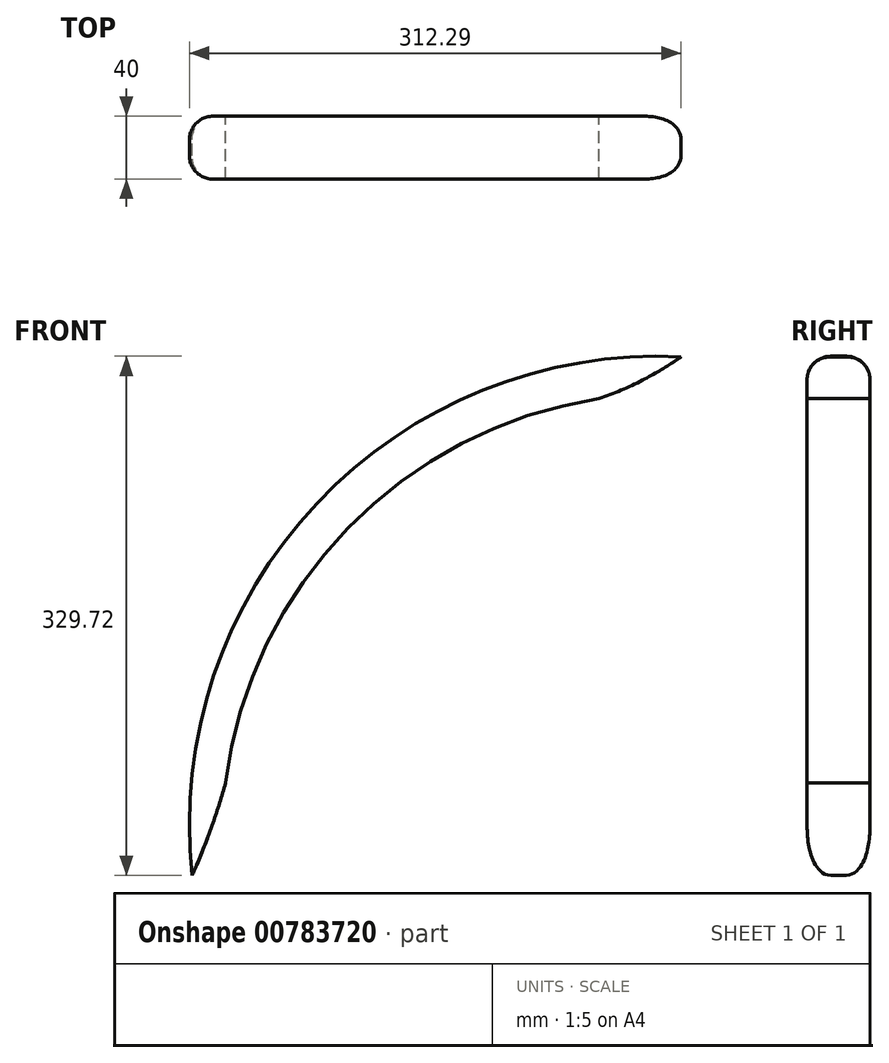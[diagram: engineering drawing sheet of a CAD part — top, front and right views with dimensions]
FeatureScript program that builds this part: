
annotation { "Feature Type Name" : "Feature", "Feature Type Description" : "" }
export const myFeature = defineFeature(function(context is Context, id is Id, definition is map)
    precondition{}
    {
        {
            var Q0;
            Q0=qCreatedBy(makeId("Front.planeOp"),FACE);
            var sketch = newSketch(context, id + "F0", { "sketchPlane" : qUnion([Q0])});
            skArc(sketch, "E0", {"start": v(-39.78, 269.99) * mm, "mid": v(-12.78, 281.45) * mm, "end": v(12.34, 296.57) * mm});
            skArc(sketch, "E1", {"start": v(-39.78, 269.99) * mm, "mid": v(-199.26, 187.75) * mm, "end": v(-276.9, 25.99) * mm});
            skArc(sketch, "E2", {"start": v(-298.2, -32.78) * mm, "mid": v(-286.5, -3.78) * mm, "end": v(-276.9, 25.99) * mm});
            skArc(sketch, "E3", {"start": v(12.34, 296.57) * mm, "mid": v(-218.9, 203.52) * mm, "end": v(-298.2, -32.78) * mm});
            skSolve(sketch);
        }
        {
            var Q0;
            Q0=makeQuery(id+"F0.imprint","IMPRINT",FACE,{"disambiguationData":[TD([[makeQuery(id+"F0.imprint","IMPRINT",EDGE,{"derivedFrom":sQuery(id+"F0.wireOp",EDGE,"E0")}),1.0]])]});
            extrude(context, id + "F1", {"entities" : qUnion([Q0]), "depth" : 40 * mm, "offsetDistance" : 25 * mm});
        }
        {
            var Q0;
            Q0=makeQuery(id+"F1.opExtrude","CAP_EDGE",EDGE,{"disambiguationData":[OSD([sQuery(id+"F0.wireOp",EDGE,"E3")])],"isStart":true});
            var Q1;
            Q1=makeQuery(id+"F1.opExtrude","CAP_EDGE",EDGE,{"disambiguationData":[OSD([sQuery(id+"F0.wireOp",EDGE,"E3")])],"isStart":false});
            fillet(context, id + "F2", {"entities" : qUnion([Q0, Q1]), "radius" : 15 * mm, "tangentPropagation" : true, "allowEdgeOverflow" : false});
        }
    });
